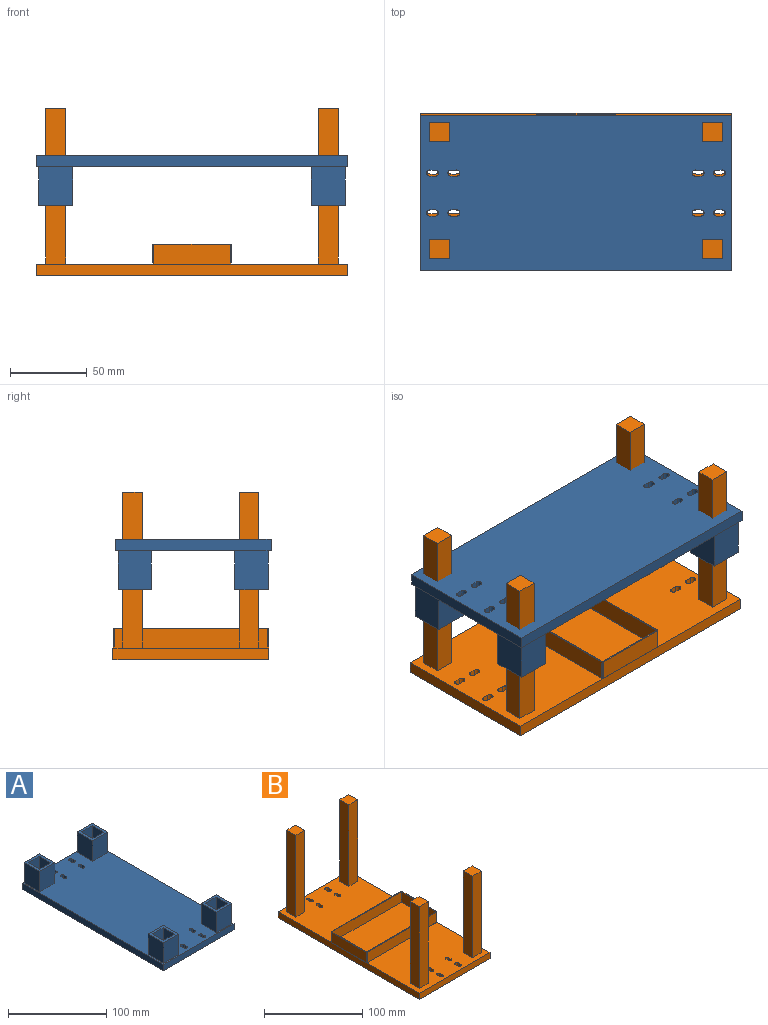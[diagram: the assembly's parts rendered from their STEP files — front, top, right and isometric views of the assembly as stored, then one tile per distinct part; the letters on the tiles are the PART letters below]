
ASSEMBLY  parts=2 mates=1
PART A: 78 faces, bbox 101.6x203.2x33 mm
  f0: plane 203.2x101.6mm, normal (0,0,1), area 18485mm2, adj f2,f3,f4,f5,f6,f7,f8,f9
  f1: plane 203.2x101.6mm, normal (0,0,-1), area 20423.8mm2, adj f2,f3,f4,f5,f6,f7,f8,f9
  f2: plane 203.2x7.62mm, normal (-1,0,0), area 1548.4mm2, adj f0,f1,f3,f5
  f3: plane 101.6x7.62mm, normal (0,-1,0), area 774.2mm2, adj f0,f1,f2,f4
  f4: plane 203.2x7.62mm, normal (1,0,0), area 1548.4mm2, adj f0,f1,f3,f5
  f5: plane 101.6x7.62mm, normal (0,1,0), area 774.2mm2, adj f0,f1,f2,f4
  f6: plane 7.62x3.73mm, normal (-1,-0.01,0), area 28.5mm2, adj f0,f1,f7,f9
  f7: cylinder r=1.99mm len=7.62mm, axis (0,0,-1), area 48.4mm2, adj f0,f1,f6,f8
  f8: plane 7.62x3.6mm, normal (1,0.01,0), area 27.4mm2, adj f0,f1,f7,f9
  f9: cylinder r=1.99mm len=7.62mm, axis (0,0,-1), area 49.3mm2, adj f0,f1,f6,f8
  f10: plane 7.62x3.73mm, normal (1,0.01,0), area 28.5mm2, adj f0,f1,f11,f13
  f11: cylinder r=1.99mm len=7.62mm, axis (0,0,-1), area 48.4mm2, adj f0,f1,f10,f12
  f12: plane 7.62x3.6mm, normal (-1,-0.01,0), area 27.4mm2, adj f0,f1,f11,f13
  f13: cylinder r=1.99mm len=7.62mm, axis (0,0,-1), area 49.3mm2, adj f0,f1,f10,f12
  f14: plane 7.62x3.73mm, normal (-1,-0.01,0), area 28.5mm2, adj f0,f1,f15,f17
  f15: cylinder r=1.99mm len=7.62mm, axis (0,0,-1), area 48.4mm2, adj f0,f1,f14,f16
  f16: plane 7.62x3.6mm, normal (1,0.01,0), area 27.4mm2, adj f0,f1,f15,f17
  f17: cylinder r=1.99mm len=7.62mm, axis (0,0,-1), area 49.3mm2, adj f0,f1,f14,f16
  f18: cylinder r=1.99mm len=7.62mm, axis (0,0,-1), area 49.3mm2, adj f0,f1,f19,f21
  f19: plane 7.62x3.6mm, normal (-1,0.01,0), area 27.4mm2, adj f0,f1,f18,f20
  f20: cylinder r=1.99mm len=7.62mm, axis (0,0,-1), area 48.4mm2, adj f0,f1,f19,f21
  f21: plane 7.62x3.73mm, normal (1,-0.01,0), area 28.5mm2, adj f0,f1,f18,f20
  f22: plane 7.62x3.6mm, normal (1,-0.01,0), area 27.4mm2, adj f0,f1,f23,f25
  f23: cylinder r=1.99mm len=7.62mm, axis (0,0,-1), area 48.4mm2, adj f0,f1,f22,f24
  f24: plane 7.62x3.73mm, normal (-1,0.01,0), area 28.5mm2, adj f0,f1,f23,f25
  f25: cylinder r=1.99mm len=7.62mm, axis (0,0,-1), area 49.3mm2, adj f0,f1,f22,f24
  f26: plane 7.62x3.6mm, normal (-1,0.01,0), area 27.4mm2, adj f0,f1,f27,f29
  f27: cylinder r=1.99mm len=7.62mm, axis (0,0,-1), area 48.4mm2, adj f0,f1,f26,f28
  f28: plane 7.62x3.73mm, normal (1,-0.01,0), area 28.5mm2, adj f0,f1,f27,f29
  f29: cylinder r=1.99mm len=7.62mm, axis (0,0,-1), area 49.3mm2, adj f0,f1,f26,f28
  f30: plane 7.62x3.6mm, normal (-1,-0.01,0), area 27.4mm2, adj f0,f1,f31,f33
  f31: cylinder r=1.99mm len=7.62mm, axis (0,0,-1), area 49.3mm2, adj f0,f1,f30,f32
  f32: plane 7.62x3.73mm, normal (1,0.01,0), area 28.5mm2, adj f0,f1,f31,f33
  f33: cylinder r=1.99mm len=7.62mm, axis (0,0,-1), area 48.4mm2, adj f0,f1,f30,f32
  f34: plane 7.62x3.6mm, normal (1,-0.01,0), area 27.4mm2, adj f0,f1,f35,f37
  f35: cylinder r=1.99mm len=7.62mm, axis (0,0,-1), area 48.4mm2, adj f0,f1,f34,f36
  f36: plane 7.62x3.73mm, normal (-1,0.01,0), area 28.5mm2, adj f0,f1,f35,f37
  f37: cylinder r=1.99mm len=7.62mm, axis (0,0,-1), area 49.3mm2, adj f0,f1,f34,f36
  f38: plane 25.4x22.34mm, normal (-1,0,0), area 567.4mm2, adj f0,f39,f45,f46
  f39: plane 25.4x21.7mm, normal (0,-1,0), area 551.2mm2, adj f0,f38,f40,f46
  f40: plane 25.4x22.34mm, normal (1,0,0), area 567.4mm2, adj f0,f39,f45,f46
  f41: plane 25.4x15.7mm, normal (0,1,0), area 398.8mm2, adj f42,f44,f46,f47
  f42: plane 25.4x16.34mm, normal (1,0,0), area 415mm2, adj f41,f43,f46,f47
  f43: plane 25.4x15.7mm, normal (0,-1,0), area 398.8mm2, adj f42,f44,f46,f47
  f44: plane 25.4x16.34mm, normal (-1,0,0), area 415mm2, adj f41,f43,f46,f47
  f45: plane 25.4x21.7mm, normal (0,1,0), area 551.2mm2, adj f0,f38,f40,f46
  f46: plane 22.34x21.7mm, normal (0,0,1), area 228.2mm2, adj f38,f39,f40,f41,f42,f43,f44,f45
  f47: plane 16.34x15.7mm, normal (0,0,1), area 256.5mm2, adj f41,f42,f43,f44
  f48: plane 25.4x15.7mm, normal (0,1,0), area 398.8mm2, adj f49,f55,f56,f57
  f49: plane 25.4x16.34mm, normal (1,0,0), area 415mm2, adj f48,f50,f56,f57
  f50: plane 25.4x15.7mm, normal (0,-1,0), area 398.8mm2, adj f49,f55,f56,f57
  f51: plane 25.4x21.7mm, normal (0,1,0), area 551.2mm2, adj f0,f52,f54,f56
  f52: plane 25.4x22.34mm, normal (-1,0,0), area 567.4mm2, adj f0,f51,f53,f56
  f53: plane 25.4x21.7mm, normal (0,-1,0), area 551.2mm2, adj f0,f52,f54,f56
  f54: plane 25.4x22.34mm, normal (1,0,0), area 567.4mm2, adj f0,f51,f53,f56
  f55: plane 25.4x16.34mm, normal (-1,0,0), area 415mm2, adj f48,f50,f56,f57
  f56: plane 22.34x21.7mm, normal (0,0,1), area 228.2mm2, adj f48,f49,f50,f51,f52,f53,f54,f55
  f57: plane 16.34x15.7mm, normal (0,0,1), area 256.5mm2, adj f48,f49,f50,f55
  f58: plane 25.4x16.34mm, normal (-1,0,0), area 415mm2, adj f59,f65,f66,f67
  f59: plane 25.4x15.7mm, normal (0,1,0), area 398.8mm2, adj f58,f60,f66,f67
  f60: plane 25.4x16.34mm, normal (1,0,0), area 415mm2, adj f59,f65,f66,f67
  f61: plane 25.4x21.7mm, normal (0,1,0), area 551.2mm2, adj f0,f62,f64,f66
  f62: plane 25.4x22.34mm, normal (-1,0,0), area 567.4mm2, adj f0,f61,f63,f66
  f63: plane 25.4x21.7mm, normal (0,-1,0), area 551.2mm2, adj f0,f62,f64,f66
  f64: plane 25.4x22.34mm, normal (1,0,0), area 567.4mm2, adj f0,f61,f63,f66
  f65: plane 25.4x15.7mm, normal (0,-1,0), area 398.8mm2, adj f58,f60,f66,f67
  f66: plane 22.34x21.7mm, normal (0,0,1), area 228.2mm2, adj f58,f59,f60,f61,f62,f63,f64,f65
  f67: plane 16.34x15.7mm, normal (0,0,1), area 256.5mm2, adj f58,f59,f60,f65
  f68: plane 25.4x15.7mm, normal (0,1,0), area 398.8mm2, adj f69,f75,f76,f77
  f69: plane 25.4x16.34mm, normal (1,0,0), area 415mm2, adj f68,f70,f76,f77
  f70: plane 25.4x15.7mm, normal (0,-1,0), area 398.8mm2, adj f69,f75,f76,f77
  f71: plane 25.4x21.7mm, normal (0,-1,0), area 551.2mm2, adj f0,f72,f74,f76
  f72: plane 25.4x22.34mm, normal (1,0,0), area 567.4mm2, adj f0,f71,f73,f76
  f73: plane 25.4x21.7mm, normal (0,1,0), area 551.2mm2, adj f0,f72,f74,f76
  f74: plane 25.4x22.34mm, normal (-1,0,0), area 567.4mm2, adj f0,f71,f73,f76
  f75: plane 25.4x16.34mm, normal (-1,0,0), area 415mm2, adj f68,f70,f76,f77
  f76: plane 22.34x21.7mm, normal (0,0,1), area 228.2mm2, adj f68,f69,f70,f71,f72,f73,f74,f75
  f77: plane 16.34x15.7mm, normal (0,0,1), area 256.5mm2, adj f68,f69,f70,f75
PART B: 72 faces, bbox 101.6x203.2x109.2 mm
  f0: plane 203.2x101.6mm, normal (0,0,1), area 14563.3mm2, adj f2,f3,f4,f5,f6,f7,f8,f9
  f1: plane 203.2x101.6mm, normal (0,0,-1), area 20423.8mm2, adj f2,f3,f4,f5,f6,f7,f8,f9
  f2: plane 203.2x7.62mm, normal (-1,0,0), area 1548.4mm2, adj f0,f1,f3,f5
  f3: plane 101.6x7.62mm, normal (0,-1,0), area 774.2mm2, adj f0,f1,f2,f4
  f4: plane 203.2x7.62mm, normal (1,0,0), area 1548.4mm2, adj f0,f1,f3,f5
  f5: plane 101.6x7.62mm, normal (0,1,0), area 774.2mm2, adj f0,f1,f2,f4
  f6: plane 7.62x3.73mm, normal (-1,-0.01,0), area 28.5mm2, adj f0,f1,f7,f9
  f7: cylinder r=1.99mm len=7.62mm, axis (0,0,-1), area 48.4mm2, adj f0,f1,f6,f8
  f8: plane 7.62x3.6mm, normal (1,0.01,0), area 27.4mm2, adj f0,f1,f7,f9
  f9: cylinder r=1.99mm len=7.62mm, axis (0,0,-1), area 49.3mm2, adj f0,f1,f6,f8
  f10: plane 7.62x3.73mm, normal (1,0.01,0), area 28.5mm2, adj f0,f1,f11,f13
  f11: cylinder r=1.99mm len=7.62mm, axis (0,0,-1), area 48.4mm2, adj f0,f1,f10,f12
  f12: plane 7.62x3.6mm, normal (-1,-0.01,0), area 27.4mm2, adj f0,f1,f11,f13
  f13: cylinder r=1.99mm len=7.62mm, axis (0,0,-1), area 49.3mm2, adj f0,f1,f10,f12
  f14: plane 7.62x3.73mm, normal (-1,-0.01,0), area 28.5mm2, adj f0,f1,f15,f17
  f15: cylinder r=1.99mm len=7.62mm, axis (0,0,-1), area 48.4mm2, adj f0,f1,f14,f16
  f16: plane 7.62x3.6mm, normal (1,0.01,0), area 27.4mm2, adj f0,f1,f15,f17
  f17: cylinder r=1.99mm len=7.62mm, axis (0,0,-1), area 49.3mm2, adj f0,f1,f14,f16
  f18: cylinder r=1.99mm len=7.62mm, axis (0,0,-1), area 49.3mm2, adj f0,f1,f19,f21
  f19: plane 7.62x3.6mm, normal (-1,0.01,0), area 27.4mm2, adj f0,f1,f18,f20
  f20: cylinder r=1.99mm len=7.62mm, axis (0,0,-1), area 48.4mm2, adj f0,f1,f19,f21
  f21: plane 7.62x3.73mm, normal (1,-0.01,0), area 28.5mm2, adj f0,f1,f18,f20
  f22: plane 7.62x3.6mm, normal (1,-0.01,0), area 27.4mm2, adj f0,f1,f23,f25
  f23: cylinder r=1.99mm len=7.62mm, axis (0,0,-1), area 48.4mm2, adj f0,f1,f22,f24
  f24: plane 7.62x3.73mm, normal (-1,0.01,0), area 28.5mm2, adj f0,f1,f23,f25
  f25: cylinder r=1.99mm len=7.62mm, axis (0,0,-1), area 49.3mm2, adj f0,f1,f22,f24
  f26: plane 7.62x3.6mm, normal (-1,0.01,0), area 27.4mm2, adj f0,f1,f27,f29
  f27: cylinder r=1.99mm len=7.62mm, axis (0,0,-1), area 48.4mm2, adj f0,f1,f26,f28
  f28: plane 7.62x3.73mm, normal (1,-0.01,0), area 28.5mm2, adj f0,f1,f27,f29
  f29: cylinder r=1.99mm len=7.62mm, axis (0,0,-1), area 49.3mm2, adj f0,f1,f26,f28
  f30: plane 7.62x3.6mm, normal (-1,-0.01,0), area 27.4mm2, adj f0,f1,f31,f33
  f31: cylinder r=1.99mm len=7.62mm, axis (0,0,-1), area 49.3mm2, adj f0,f1,f30,f32
  f32: plane 7.62x3.73mm, normal (1,0.01,0), area 28.5mm2, adj f0,f1,f31,f33
  f33: cylinder r=1.99mm len=7.62mm, axis (0,0,-1), area 48.4mm2, adj f0,f1,f30,f32
  f34: plane 7.62x3.6mm, normal (1,-0.01,0), area 27.4mm2, adj f0,f1,f35,f37
  f35: cylinder r=1.99mm len=7.62mm, axis (0,0,-1), area 48.4mm2, adj f0,f1,f34,f36
  f36: plane 7.62x3.73mm, normal (-1,0.01,0), area 28.5mm2, adj f0,f1,f35,f37
  f37: cylinder r=1.99mm len=7.62mm, axis (0,0,-1), area 49.3mm2, adj f0,f1,f34,f36
  f38: plane 101.6x13.11mm, normal (-1,0,0), area 1331.5mm2, adj f0,f39,f41,f42
  f39: plane 101.6x12.7mm, normal (0,-1,0), area 1290.3mm2, adj f0,f38,f40,f42
  f40: plane 101.6x13.11mm, normal (1,0,0), area 1331.5mm2, adj f0,f39,f41,f42
  f41: plane 101.6x12.7mm, normal (0,1,0), area 1290.3mm2, adj f0,f38,f40,f42
  f42: plane 13.11x12.7mm, normal (0,0,1), area 166.4mm2, adj f38,f39,f40,f41
  f43: plane 101.6x13.11mm, normal (1,0,0), area 1331.5mm2, adj f0,f44,f46,f47
  f44: plane 101.6x12.7mm, normal (0,1,0), area 1290.3mm2, adj f0,f43,f45,f47
  f45: plane 101.6x13.11mm, normal (-1,0,0), area 1331.5mm2, adj f0,f44,f46,f47
  f46: plane 101.6x12.7mm, normal (0,-1,0), area 1290.3mm2, adj f0,f43,f45,f47
  f47: plane 13.11x12.7mm, normal (0,0,1), area 166.4mm2, adj f43,f44,f45,f46
  f48: plane 101.6x13.11mm, normal (-1,0,0), area 1331.5mm2, adj f0,f49,f51,f52
  f49: plane 101.6x12.7mm, normal (0,-1,0), area 1290.3mm2, adj f0,f48,f50,f52
  f50: plane 101.6x13.11mm, normal (1,0,0), area 1331.5mm2, adj f0,f49,f51,f52
  f51: plane 101.6x12.7mm, normal (0,1,0), area 1290.3mm2, adj f0,f48,f50,f52
  f52: plane 13.11x12.7mm, normal (0,0,1), area 166.4mm2, adj f48,f49,f50,f51
  f53: plane 101.6x13.11mm, normal (-1,0,0), area 1331.5mm2, adj f0,f54,f56,f57
  f54: plane 101.6x12.7mm, normal (0,-1,0), area 1290.3mm2, adj f0,f53,f55,f57
  f55: plane 101.6x13.11mm, normal (1,0,0), area 1331.5mm2, adj f0,f54,f56,f57
  f56: plane 101.6x12.7mm, normal (0,1,0), area 1290.3mm2, adj f0,f53,f55,f57
  f57: plane 13.11x12.7mm, normal (0,0,1), area 166.4mm2, adj f53,f54,f55,f56
  f58: plane 12.95x0.78mm, normal (-0.6,-0.8,0), area 12.6mm2, adj f0,f59,f69,f70
  f59: plane 100x12.95mm, normal (0,-1,0), area 1295.4mm2, adj f0,f58,f60,f70
  f60: plane 12.95x0.76mm, normal (0.61,-0.79,0), area 12.4mm2, adj f0,f59,f61,f70
  f61: plane 50x12.95mm, normal (1,0,0), area 647.7mm2, adj f0,f60,f62,f70
  f62: plane 12.95x0.76mm, normal (0.61,0.79,0), area 12.4mm2, adj f0,f61,f63,f70
  f63: plane 100x12.95mm, normal (0,1,0), area 1295.4mm2, adj f0,f62,f64,f70
  f64: plane 12.95x0.78mm, normal (-0.6,0.8,0), area 12.6mm2, adj f0,f63,f69,f70
  f65: plane 100x12.95mm, normal (0,1,0), area 1295.4mm2, adj f66,f68,f70,f71
  f66: plane 50x12.95mm, normal (1,0,0), area 647.7mm2, adj f65,f67,f70,f71
  f67: plane 100x12.95mm, normal (0,-1,0), area 1295.4mm2, adj f66,f68,f70,f71
  f68: plane 50x12.95mm, normal (-1,0,0), area 647.7mm2, adj f65,f67,f70,f71
  f69: plane 50x12.95mm, normal (-1,0,0), area 647.7mm2, adj f0,f58,f64,f70
  f70: plane 101.54x51.17mm, normal (0,0,1), area 194.7mm2, adj f58,f59,f60,f61,f62,f63,f64,f65
  f71: plane 100x50mm, normal (0,0,1), area 5000mm2, adj f65,f66,f67,f68
PLACE A rot(axis=(-0.71,0.71,0),180deg) t=(78.79,-150.97,18)mm
PLACE B rot(axis=(0,0,1),90deg) t=(78.79,-149.47,-60.74)mm
MATE slider A.f69 <-> B.f50  axis (0,-1,0) through (167.69,-105.02,-2.32)mm
